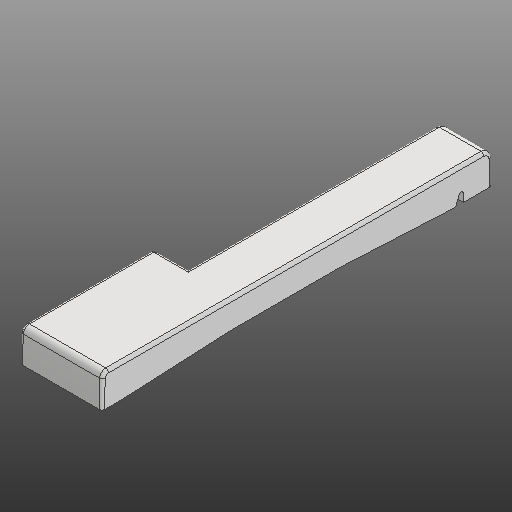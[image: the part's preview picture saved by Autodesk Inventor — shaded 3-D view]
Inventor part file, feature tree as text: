
AUTODESK INVENTOR PART (.ipt)
format: ipt  version: 2020 (Build 240168000, 168)  size: 322,048 bytes
history: native  units: in
note: dims shown in document units (in); Inventor stores cm internally (conversion verified against a paired STEP export)
features: extrude x4, other x3, fillet x2
ambient origin geometry x8: Origin, YZ Plane, XZ Plane, XY Plane, X Axis, Y Axis, Z Axis, Center Point
bodies: Solid1 (feature_tree)
feature tree (9):
  other  "Slot Start Plane"
  other  "Key Profile"
  extrude  "Upper (u)"  TaperAngle=0.0deg  [1 undecoded]
  extrude  "Lower (d)"  TaperAngle=0.0deg  [1 undecoded]
  extrude  "Protrusion Cutout"  Depth=0.0591in
  fillet  "Front Fillet"  Radius=0.1374in
  extrude  "Slot"  [1 undecoded]
  fillet  "Edge Softening"  Radius=0.0787in
  other  "Slot Sketch"
note: 3 required parameter values undecoded (feature->parameter linkage not recoverable at this tier; creation-order binding heuristic only, values carry confidence <= 0.55)
